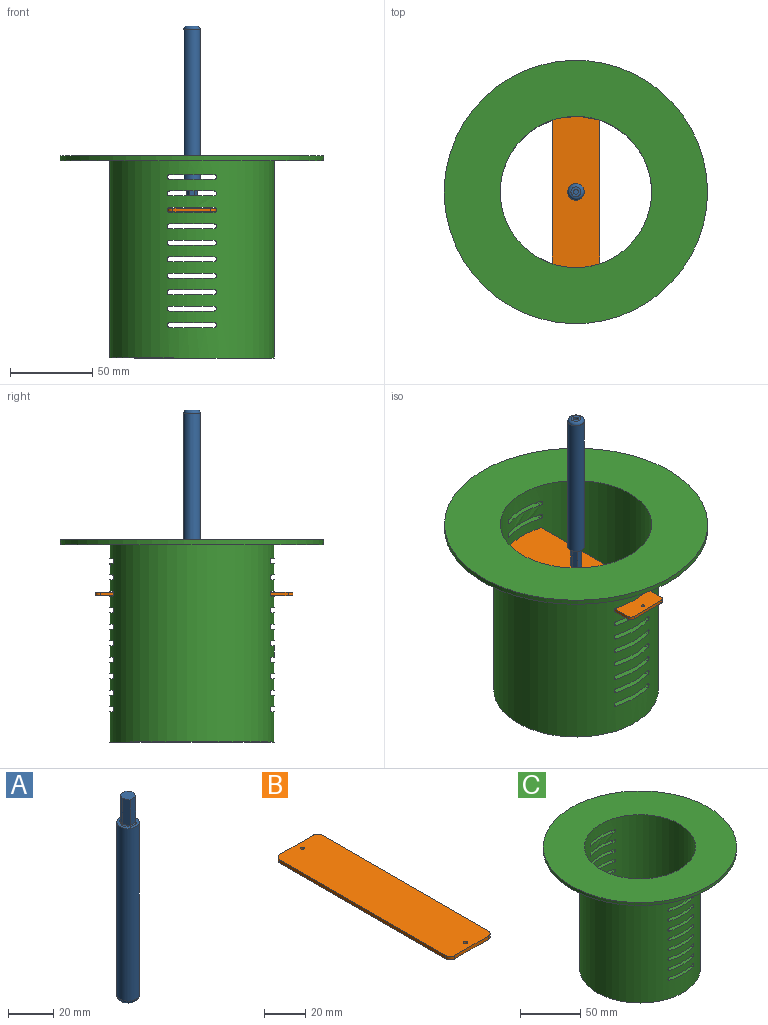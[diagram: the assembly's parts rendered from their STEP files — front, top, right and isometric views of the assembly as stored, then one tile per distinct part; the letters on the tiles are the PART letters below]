
ASSEMBLY  parts=3 mates=2
PART A: 19 faces, bbox 10.8x10.8x110 mm
  f0: cylinder r=5mm len=93.5mm, axis (0,0,-1), area 2937.4mm2, adj f1,f16
  f1: plane 10x10mm, normal (0,0,1), area 36.1mm2, adj f0,f10,f11,f12,f13,f14,f15
  f2: plane 6x6mm, normal (0,0,-1), area 21.2mm2, adj f16,f17
  f3: plane 14x3mm, normal (0.87,0.5,0), area 48.5mm2, adj f4,f8,f9,f12
  f4: plane 14x3.46mm, normal (0,1,0), area 48.5mm2, adj f3,f5,f9,f10
  f5: plane 14x3mm, normal (-0.87,0.5,0), area 48.5mm2, adj f4,f6,f9,f11
  f6: plane 14x3mm, normal (-0.87,-0.5,0), area 48.5mm2, adj f5,f7,f9,f13
  f7: plane 14x3.46mm, normal (0,-1,0), area 48.5mm2, adj f6,f8,f9,f15
  f8: plane 14x3mm, normal (0.87,-0.5,0), area 48.5mm2, adj f3,f7,f9,f14
  f9: plane 6.93x6mm, normal (0,0,1), area 31.2mm2, adj f3,f4,f5,f6,f7,f8
  f10: cylinder r=0.5mm len=4.04mm, axis (-1,0,0), area 2.9mm2, adj f1,f4,f11,f12
  f11: cylinder r=0.5mm len=3.75mm, axis (-0.5,-0.87,0), area 2.9mm2, adj f1,f5,f10,f13
  f12: cylinder r=0.5mm len=3.75mm, axis (-0.5,0.87,0), area 2.9mm2, adj f1,f3,f10,f14
  f13: cylinder r=0.5mm len=3.75mm, axis (0.5,-0.87,0), area 2.9mm2, adj f1,f6,f11,f15
  f14: cylinder r=0.5mm len=3.75mm, axis (0.5,0.87,0), area 2.9mm2, adj f1,f8,f12,f15
  f15: cylinder r=0.5mm len=4.04mm, axis (1,0,0), area 2.9mm2, adj f1,f7,f13,f14
  f16: torus R=3mm, axis (0,0,1), area 84.4mm2, adj f0,f2
  f17: cylinder r=1.5mm len=3mm, axis (0,0,-1), area 18.8mm2, adj f2,f18
  f18: plane 3x3mm, normal (0,0,-1), area 7.1mm2, adj f17
PART B: 12 faces, bbox 29x120x2 mm
  f0: plane 120x29mm, normal (0,0,1), area 3466mm2, adj f2,f3,f4,f5,f6,f7,f8,f9
  f1: plane 120x29mm, normal (0,0,-1), area 3466mm2, adj f2,f3,f4,f5,f6,f7,f8,f9
  f2: plane 23x2mm, normal (0,1,0), area 46mm2, adj f0,f1,f6,f9
  f3: plane 114x2mm, normal (-1,0,0), area 228mm2, adj f0,f1,f6,f7
  f4: plane 23x2mm, normal (0,-1,0), area 46mm2, adj f0,f1,f7,f8
  f5: plane 114x2mm, normal (1,0,0), area 228mm2, adj f0,f1,f8,f9
  f6: cylinder r=3mm len=3mm, axis (0,0,-1), area 9.4mm2, adj f0,f1,f2,f3
  f7: cylinder r=3mm len=3mm, axis (0,0,-1), area 9.4mm2, adj f0,f1,f3,f4
  f8: cylinder r=3mm len=3mm, axis (0,0,-1), area 9.4mm2, adj f0,f1,f4,f5
  f9: cylinder r=3mm len=3mm, axis (0,0,-1), area 9.4mm2, adj f0,f1,f2,f5
  f10: cylinder r=1mm len=2mm, axis (0,0,1), area 12.6mm2, adj f0,f1
  f11: cylinder r=1mm len=2mm, axis (0,0,1), area 12.6mm2, adj f0,f1
PART C: 86 faces, bbox 160x160x123 mm
  f0: cylinder r=50mm len=120mm, axis (0,0,-1), area 35911.3mm2, adj f2,f3,f6,f7,f8,f9,f10,f11
  f1: cylinder r=46mm len=123mm, axis (0,0,1), area 33757.2mm2, adj f2,f4,f6,f7,f8,f9,f10,f11
  f2: plane 100x100mm, normal (0,0,-1), area 1206.4mm2, adj f0,f1
  f3: plane 160x160mm, normal (0,0,-1), area 12252.2mm2, adj f0,f5
  f4: plane 160x160mm, normal (0,0,1), area 13458.6mm2, adj f1,f5
  f5: cylinder r=80mm len=160mm, axis (0,0,-1), area 1508mm2, adj f3,f4
  f6: plane 27x6.03mm, normal (0,0,1), area 109.5mm2, adj f0,f1,f7,f9
  f7: cylinder r=1.5mm len=4.66mm, axis (0,-1,0), area 19.8mm2, adj f0,f1,f6,f8
  f8: plane 27x6.03mm, normal (0,0,-1), area 109.5mm2, adj f0,f1,f7,f9
  f9: cylinder r=1.5mm len=4.66mm, axis (0,-1,0), area 19.8mm2, adj f0,f1,f6,f8
  f10: cylinder r=1.5mm len=4.66mm, axis (0,-1,0), area 19.8mm2, adj f0,f1,f11,f13
  f11: plane 27x6.03mm, normal (0,0,-1), area 109.5mm2, adj f0,f1,f10,f12
  f12: cylinder r=1.5mm len=4.66mm, axis (0,-1,0), area 19.8mm2, adj f0,f1,f11,f13
  f13: plane 27x6.03mm, normal (0,0,1), area 109.5mm2, adj f0,f1,f10,f12
  f14: cylinder r=1.5mm len=4.66mm, axis (0,-1,0), area 19.8mm2, adj f0,f1,f15,f17
  f15: plane 27x6.03mm, normal (0,0,-1), area 109.5mm2, adj f0,f1,f14,f16
  f16: cylinder r=1.5mm len=4.66mm, axis (0,-1,0), area 19.8mm2, adj f0,f1,f15,f17
  f17: plane 27x6.03mm, normal (0,0,1), area 109.5mm2, adj f0,f1,f14,f16
  f18: plane 27x6.03mm, normal (0,0,1), area 109.5mm2, adj f0,f1,f19,f21
  f19: cylinder r=1.5mm len=4.66mm, axis (0,-1,0), area 19.8mm2, adj f0,f1,f18,f20
  f20: plane 27x6.03mm, normal (0,0,-1), area 109.5mm2, adj f0,f1,f19,f21
  f21: cylinder r=1.5mm len=4.66mm, axis (0,-1,0), area 19.8mm2, adj f0,f1,f18,f20
  f22: cylinder r=1.5mm len=4.66mm, axis (0,-1,0), area 19.8mm2, adj f0,f1,f23,f25
  f23: plane 27x6.03mm, normal (0,0,-1), area 109.5mm2, adj f0,f1,f22,f24
  f24: cylinder r=1.5mm len=4.66mm, axis (0,-1,0), area 19.8mm2, adj f0,f1,f23,f25
  f25: plane 27x6.03mm, normal (0,0,1), area 109.5mm2, adj f0,f1,f22,f24
  f26: plane 27x6.03mm, normal (0,0,1), area 109.5mm2, adj f0,f1,f27,f29
  f27: cylinder r=1.5mm len=4.66mm, axis (0,-1,0), area 19.8mm2, adj f0,f1,f26,f28
  f28: plane 27x6.03mm, normal (0,0,-1), area 109.5mm2, adj f0,f1,f27,f29
  f29: cylinder r=1.5mm len=4.66mm, axis (0,-1,0), area 19.8mm2, adj f0,f1,f26,f28
  f30: cylinder r=1.5mm len=4.66mm, axis (0,-1,0), area 19.8mm2, adj f0,f1,f31,f33
  f31: plane 27x6.03mm, normal (0,0,-1), area 109.5mm2, adj f0,f1,f30,f32
  f32: cylinder r=1.5mm len=4.66mm, axis (0,-1,0), area 19.8mm2, adj f0,f1,f31,f33
  f33: plane 27x6.03mm, normal (0,0,1), area 109.5mm2, adj f0,f1,f30,f32
  f34: plane 27x6.03mm, normal (0,0,1), area 109.5mm2, adj f0,f1,f35,f37
  f35: cylinder r=1.5mm len=4.66mm, axis (0,-1,0), area 19.8mm2, adj f0,f1,f34,f36
  f36: plane 27x6.03mm, normal (0,0,-1), area 109.5mm2, adj f0,f1,f35,f37
  f37: cylinder r=1.5mm len=4.66mm, axis (0,-1,0), area 19.8mm2, adj f0,f1,f34,f36
  f38: cylinder r=1.5mm len=4.66mm, axis (0,-1,0), area 19.8mm2, adj f0,f1,f39,f41
  f39: plane 27x6.03mm, normal (0,0,-1), area 109.5mm2, adj f0,f1,f38,f40
  f40: cylinder r=1.5mm len=4.66mm, axis (0,-1,0), area 19.8mm2, adj f0,f1,f39,f41
  f41: plane 27x6.03mm, normal (0,0,1), area 109.5mm2, adj f0,f1,f38,f40
  f42: plane 27x6.03mm, normal (0,0,1), area 109.5mm2, adj f0,f1,f43,f45
  f43: cylinder r=1.5mm len=4.66mm, axis (0,-1,0), area 19.8mm2, adj f0,f1,f42,f44
  f44: plane 27x6.03mm, normal (0,0,-1), area 109.5mm2, adj f0,f1,f43,f45
  f45: cylinder r=1.5mm len=4.66mm, axis (0,-1,0), area 19.8mm2, adj f0,f1,f42,f44
  f46: cylinder r=1.5mm len=4.66mm, axis (0,-1,0), area 19.8mm2, adj f0,f1,f47,f49
  f47: plane 27x6.03mm, normal (0,0,-1), area 109.5mm2, adj f0,f1,f46,f48
  f48: cylinder r=1.5mm len=4.66mm, axis (0,-1,0), area 19.8mm2, adj f0,f1,f47,f49
  f49: plane 27x6.03mm, normal (0,0,1), area 109.5mm2, adj f0,f1,f46,f48
  f50: plane 27x6.03mm, normal (0,0,1), area 109.5mm2, adj f0,f1,f51,f53
  f51: cylinder r=1.5mm len=4.66mm, axis (0,-1,0), area 19.8mm2, adj f0,f1,f50,f52
  f52: plane 27x6.03mm, normal (0,0,-1), area 109.5mm2, adj f0,f1,f51,f53
  f53: cylinder r=1.5mm len=4.66mm, axis (0,-1,0), area 19.8mm2, adj f0,f1,f50,f52
  f54: cylinder r=1.5mm len=4.66mm, axis (0,-1,0), area 19.8mm2, adj f0,f1,f55,f57
  f55: plane 27x6.03mm, normal (0,0,-1), area 109.5mm2, adj f0,f1,f54,f56
  f56: cylinder r=1.5mm len=4.66mm, axis (0,-1,0), area 19.8mm2, adj f0,f1,f55,f57
  f57: plane 27x6.03mm, normal (0,0,1), area 109.5mm2, adj f0,f1,f54,f56
  f58: plane 27x6.03mm, normal (0,0,1), area 109.5mm2, adj f0,f1,f59,f61
  f59: cylinder r=1.5mm len=4.66mm, axis (0,-1,0), area 19.8mm2, adj f0,f1,f58,f60
  f60: plane 27x6.03mm, normal (0,0,-1), area 109.5mm2, adj f0,f1,f59,f61
  f61: cylinder r=1.5mm len=4.66mm, axis (0,-1,0), area 19.8mm2, adj f0,f1,f58,f60
  f62: cylinder r=1.5mm len=4.66mm, axis (0,-1,0), area 19.8mm2, adj f0,f1,f63,f65
  f63: plane 27x6.03mm, normal (0,0,-1), area 109.5mm2, adj f0,f1,f62,f64
  f64: cylinder r=1.5mm len=4.66mm, axis (0,-1,0), area 19.8mm2, adj f0,f1,f63,f65
  f65: plane 27x6.03mm, normal (0,0,1), area 109.5mm2, adj f0,f1,f62,f64
  f66: plane 27x6.03mm, normal (0,0,1), area 109.5mm2, adj f0,f1,f67,f69
  f67: cylinder r=1.5mm len=4.66mm, axis (0,-1,0), area 19.8mm2, adj f0,f1,f66,f68
  f68: plane 27x6.03mm, normal (0,0,-1), area 109.5mm2, adj f0,f1,f67,f69
  f69: cylinder r=1.5mm len=4.66mm, axis (0,-1,0), area 19.8mm2, adj f0,f1,f66,f68
  f70: cylinder r=1.5mm len=4.66mm, axis (0,-1,0), area 19.8mm2, adj f0,f1,f71,f73
  f71: plane 27x6.03mm, normal (0,0,-1), area 109.5mm2, adj f0,f1,f70,f72
  f72: cylinder r=1.5mm len=4.66mm, axis (0,-1,0), area 19.8mm2, adj f0,f1,f71,f73
  f73: plane 27x6.03mm, normal (0,0,1), area 109.5mm2, adj f0,f1,f70,f72
  f74: plane 27x6.03mm, normal (0,0,1), area 109.5mm2, adj f0,f1,f75,f77
  f75: cylinder r=1.5mm len=4.66mm, axis (0,-1,0), area 19.8mm2, adj f0,f1,f74,f76
  f76: plane 27x6.03mm, normal (0,0,-1), area 109.5mm2, adj f0,f1,f75,f77
  f77: cylinder r=1.5mm len=4.66mm, axis (0,-1,0), area 19.8mm2, adj f0,f1,f74,f76
  f78: cylinder r=1.5mm len=4.66mm, axis (0,-1,0), area 19.8mm2, adj f0,f1,f79,f81
  f79: plane 27x6.03mm, normal (0,0,1), area 109.5mm2, adj f0,f1,f78,f80
  f80: cylinder r=1.5mm len=4.66mm, axis (0,-1,0), area 19.8mm2, adj f0,f1,f79,f81
  f81: plane 27x6.03mm, normal (0,0,-1), area 109.5mm2, adj f0,f1,f78,f80
  f82: plane 27x6.03mm, normal (0,0,-1), area 109.5mm2, adj f0,f1,f83,f85
  f83: cylinder r=1.5mm len=4.66mm, axis (0,-1,0), area 19.8mm2, adj f0,f1,f82,f84
  f84: plane 27x6.03mm, normal (0,0,1), area 109.5mm2, adj f0,f1,f83,f85
  f85: cylinder r=1.5mm len=4.66mm, axis (0,-1,0), area 19.8mm2, adj f0,f1,f82,f84
PLACE A rot(axis=(1,0,0),180deg) t=(23.1,-194.82,196.73)mm
PLACE B rot(axis=(-0.84,-0.04,-0.54),0deg) t=(8.6,-180.58,83.94)mm
PLACE C t=(23.1,-194.82,-5.05)mm
MATE slider A.f0 <-> C.f1  axis (0,0,-1) through (23.1,-194.82,86.73)mm
MATE slider C.f17 <-> B.f1  axis (0,0,1) through (23.1,-242.17,93.45)mm
